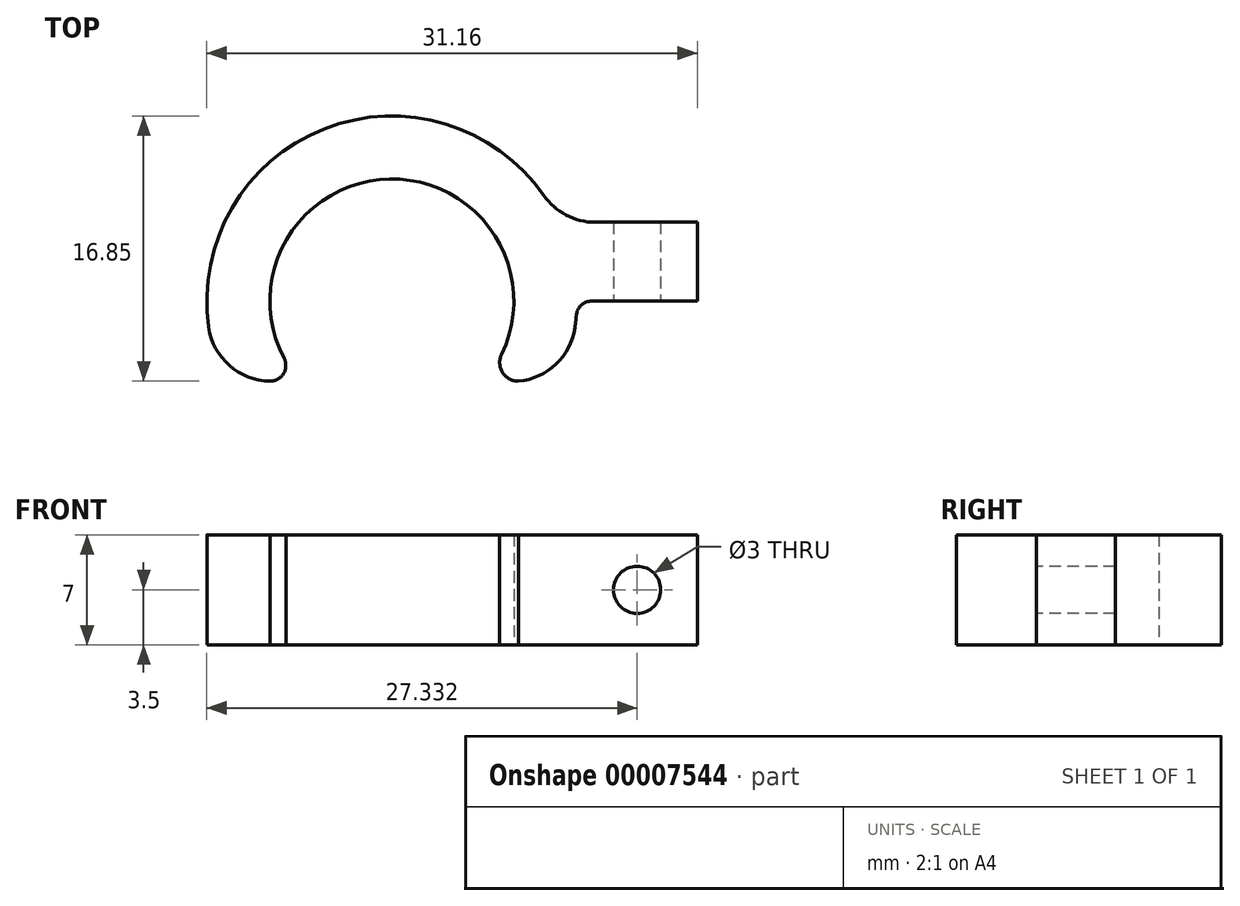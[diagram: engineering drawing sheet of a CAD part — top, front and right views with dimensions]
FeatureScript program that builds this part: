
annotation { "Feature Type Name" : "Feature", "Feature Type Description" : "" }
export const myFeature = defineFeature(function(context is Context, id is Id, definition is map)
    precondition{}
    {
        {
            var Q0;
            Q0=qCreatedBy(makeId("Top.planeOp"),FACE);
            var sketch = newSketch(context, id + "F0", { "sketchPlane" : qUnion([Q0])});
            skArc(sketch, "E0", {"start": v(-140.2, -34.05) * mm, "mid": v(-147.31, -22.91) * mm, "end": v(-154.02, -34.3) * mm});
            skArc(sketch, "E1.0", {"start": v(-136.59, -35.76) * mm, "mid": v(-147.18, -18.91) * mm, "end": v(-157.76, -35.76) * mm});
            skLineSegment(sketch, "E2", {"start": v(-157.76, -35.76) * mm, "end": v(-154.9, -35.76) * mm});
            skLineSegment(sketch, "E3.trimOffspring", {"start": v(-139.13, -35.76) * mm, "end": v(-136.59, -35.76) * mm});
            skPoint(sketch, "E4.visualSharp", {"position": v(-141.34, -35.76) * mm});
            skArc(sketch, "E4.filletArc", {"start": v(-140.2, -34.05) * mm, "mid": v(-140.14, -35.2) * mm, "end": v(-139.13, -35.76) * mm});
            skPoint(sketch, "E5.visualSharp", {"position": v(-153.02, -35.76) * mm});
            skArc(sketch, "E5.filletArc", {"start": v(-154.9, -35.76) * mm, "mid": v(-154.05, -35.27) * mm, "end": v(-154.02, -34.3) * mm});
            skLineSegment(sketch, "E6", {"start": v(-147.18, -30.66) * mm, "end": v(-87.68, -30.66) * mm});
            skLineSegment(sketch, "E7", {"start": v(-136.54, -25.66) * mm, "end": v(-87.68, -25.66) * mm});
            skLineSegment(sketch, "E8", {"start": v(-127.77, -30.66) * mm, "end": v(-127.77, -25.66) * mm});
            skSolve(sketch);
        }
        {
            var Q0;
            Q0=makeQuery(id+"F0.imprint","IMPRINT",FACE,{"disambiguationData":[TD([[makeQuery(id+"F0.imprint","IMPRINT",EDGE,{"derivedFrom":sQuery(id+"F0.wireOp",EDGE,"dac25c50-b9e0-4085-8398-18163ec7bd44.top")}),-1.0]])]});
            var Q1;
            {var subQ0=sQuery(id+"F0.wireOp",EDGE,"dac25c50-b9e0-4085-8398-18163ec7bd44.bottom");Q1=makeQuery(id+"F0.imprint","IMPRINT",FACE,{"disambiguationData":[TD([[makeQuery(id+"F0.imprint","IMPRINT",EDGE,{"derivedFrom":subQ0}),1.0]])]});}
            var Q2;
            Q2=makeQuery(id+"F0.imprint","IMPRINT",FACE,{"disambiguationData":[TD([[makeQuery(id+"F0.imprint","IMPRINT",EDGE,{"derivedFrom":sQuery(id+"F0.wireOp",EDGE,"E0")}),-1.0]])]});
            var Q3;
            {var subQ6=sQuery(id+"F0.wireOp",EDGE,"E2");Q3=makeQuery(id+"F0.imprint","IMPRINT",FACE,{"disambiguationData":[TD([[makeQuery(id+"F0.imprint","IMPRINT",EDGE,{"derivedFrom":subQ6}),1.0]])]});}
            var Q4;
            {var subQ1=sQuery(id+"F0.wireOp",EDGE,"E8");Q4=makeQuery(id+"F0.imprint","IMPRINT",FACE,{"disambiguationData":[TD([[makeQuery(id+"F0.imprint","IMPRINT",EDGE,{"derivedFrom":subQ1}),1.0]])]});}
            extrude(context, id + "F1", {"entities" : qUnion([Q0, Q1, Q2, Q3, Q4]), "depth" : 7 * mm});
        }
        {
            var Q0;
            Q0=makeQuery(id+"F1.opExtrude","SWEPT_FACE",FACE,{"disambiguationData":[OSD([sQuery(id+"F0.wireOp",EDGE,"E6")])]});
            var sketch = newSketch(context, id + "F2", { "sketchPlane" : qUnion([Q0])});
            skCircle(sketch, "E9", {"center": v(-131.6, 3.5) * mm, "radius": 1.5 * mm});
            skLineSegment(sketch, "E10", {"start": v(-131.6, 7) * mm, "end": v(-131.6, 0) * mm, "construction": true});
            skSolve(sketch);
        }
        {
            var Q0;
            Q0=makeQuery(id+"F2.imprint","IMPRINT",FACE,{"disambiguationData":[TD([[makeQuery(id+"F2.imprint","IMPRINT",EDGE,{"derivedFrom":sQuery(id+"F2.wireOp",EDGE,"E9")}),1.0]])]});
            extrude(context, id + "F3", {"entities" : qUnion([Q0]), "operationType" : NewBodyOperationType.REMOVE, "oppositeDirection" : true, "depth" : 25 * mm});
        }
        {
            var Q0;
            Q0=makeQuery(id+"F1.opExtrude","SWEPT_EDGE",EDGE,{"disambiguationData":[OSD([sQuery(id+"F0.wireOp",EDGE,"E1.0"),sQuery(id+"F0.wireOp",EDGE,"E3.trimOffspring")])]});
            var Q1;
            Q1=makeQuery(id+"F1.opExtrude","SWEPT_EDGE",EDGE,{"disambiguationData":[OSD([sQuery(id+"F0.wireOp",EDGE,"E1.0"),sQuery(id+"F0.wireOp",EDGE,"E2")])]});
            var Q2;
            Q2=makeQuery(id+"F1.opExtrude","SWEPT_EDGE",EDGE,{"disambiguationData":[OSD([sQuery(id+"F0.wireOp",EDGE,"E1.0"),sQuery(id+"F0.wireOp",EDGE,"E7")])]});
            fillet(context, id + "F4", {"entities" : qUnion([Q0, Q1, Q2]), "radius" : 4 * mm, "tangentPropagation" : true, "allowEdgeOverflow" : false});
        }
        {
            var Q0;
            Q0=makeQuery(id+"F1.opExtrude","SWEPT_EDGE",EDGE,{"disambiguationData":[OSD([sQuery(id+"F0.wireOp",EDGE,"E1.0"),sQuery(id+"F0.wireOp",EDGE,"E6")])]});
            fillet(context, id + "F5", {"entities" : qUnion([Q0]), "radius" : 1 * mm, "tangentPropagation" : true, "allowEdgeOverflow" : false});
        }
    });
